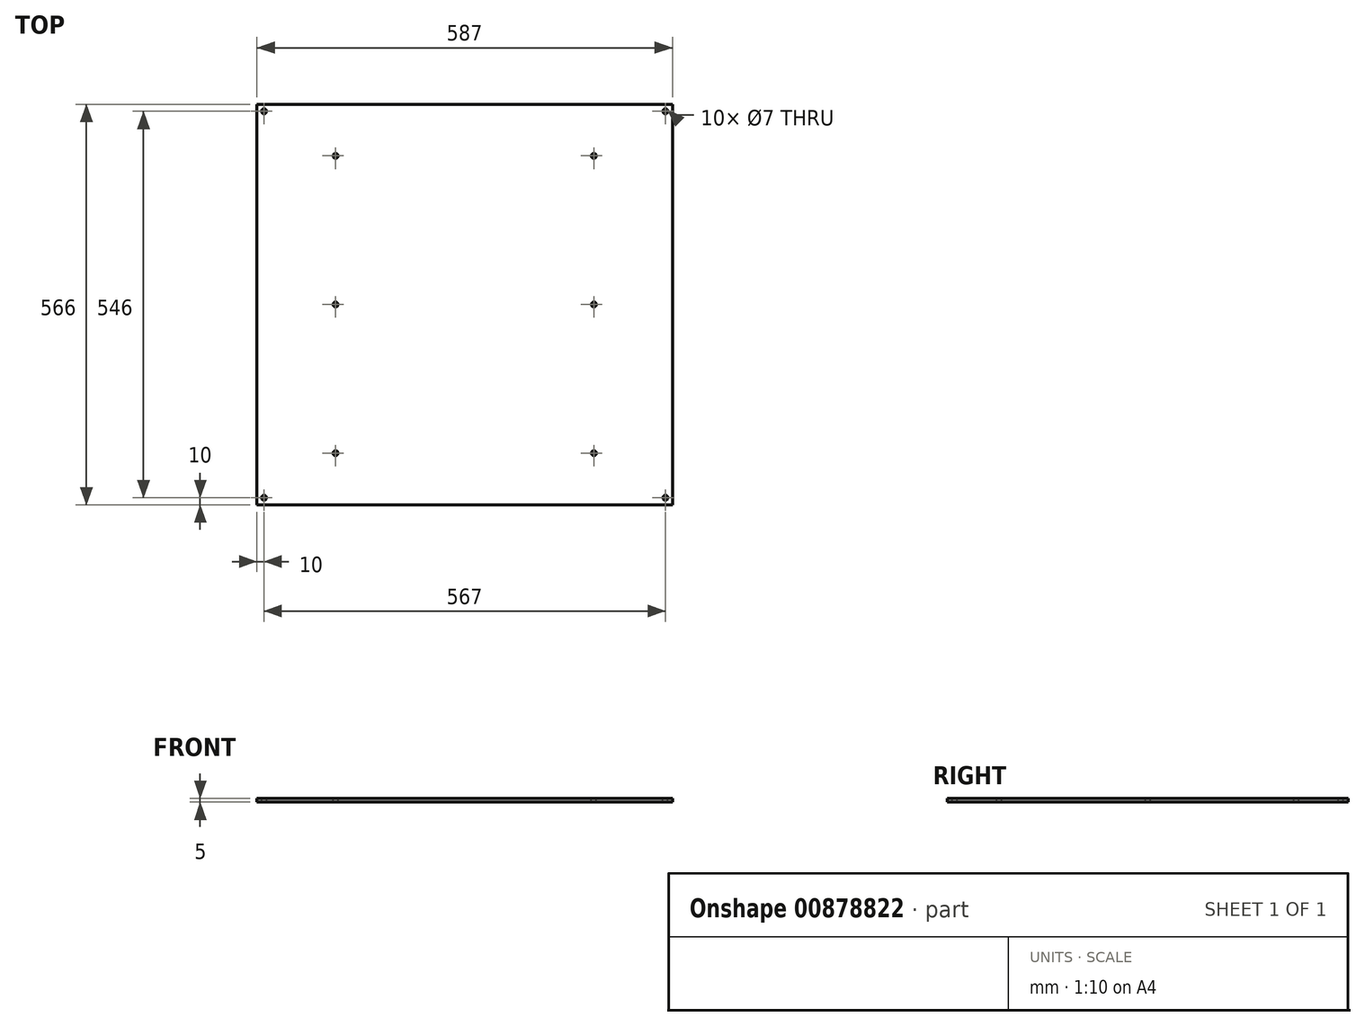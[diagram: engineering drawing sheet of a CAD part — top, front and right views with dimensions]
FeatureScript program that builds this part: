
annotation { "Feature Type Name" : "Feature", "Feature Type Description" : "" }
export const myFeature = defineFeature(function(context is Context, id is Id, definition is map)
    precondition{}
    {
        {
            var Q0;
            Q0=qCreatedBy(makeId("Top.planeOp"),FACE);
            var sketch = newSketch(context, id + "F0", { "sketchPlane" : qUnion([Q0])});
            skLineSegment(sketch, "E0.bottom", {"start": v(0, 0) * mm, "end": v(587, 0) * mm});
            skLineSegment(sketch, "E0.top", {"start": v(0, 566) * mm, "end": v(587, 566) * mm});
            skLineSegment(sketch, "E0.left", {"start": v(0, 0) * mm, "end": v(0, 566) * mm});
            skLineSegment(sketch, "E0.right", {"start": v(587, 0) * mm, "end": v(587, 566) * mm});
            skSolve(sketch);
        }
        {
            var Q0;
            Q0=makeQuery(id+"F0.imprint","IMPRINT",FACE,{"disambiguationData":[TD([[makeQuery(id+"F0.imprint","IMPRINT",EDGE,{"derivedFrom":sQuery(id+"F0.wireOp",EDGE,"E0.bottom")}),1.0]])]});
            extrude(context, id + "F1", {"entities" : qUnion([Q0]), "depth" : 5 * mm, "offsetDistance" : 25 * mm});
        }
        {
            var Q0;
            Q0=makeQuery(id+"F1.opExtrude","CAP_FACE",FACE,{"disambiguationData":[OSD([sQuery(id+"F0.wireOp",EDGE,"E0.bottom"),sQuery(id+"F0.wireOp",EDGE,"E0.top"),sQuery(id+"F0.wireOp",EDGE,"E0.left"),sQuery(id+"F0.wireOp",EDGE,"E0.right")])],"isStart":false});
            var sketch = newSketch(context, id + "F2", { "sketchPlane" : qUnion([Q0])});
            skCircle(sketch, "E1", {"center": v(10, 10) * mm, "radius": 3.5 * mm});
            skCircle(sketch, "E2", {"center": v(577, 10) * mm, "radius": 3.5 * mm});
            skCircle(sketch, "E3", {"center": v(10, 556) * mm, "radius": 3.5 * mm});
            skCircle(sketch, "E4", {"center": v(577, 556) * mm, "radius": 3.5 * mm});
            skSolve(sketch);
        }
        {
            var Q0;
            Q0=sQuery(id+"F2.wireOp",VERTEX,"E3.center");
            var Q1;
            Q1=sQuery(id+"F2.wireOp",VERTEX,"E4.center");
            var Q2;
            Q2=sQuery(id+"F2.wireOp",VERTEX,"E2.center");
            var Q3;
            Q3=sQuery(id+"F2.wireOp",VERTEX,"E1.center");
            var Q4;
            Q4=makeQuery(id+"F1.opExtrude","SWEPT_BODY",BODY,{"disambiguationData":[OSD([sQuery(id+"F0.wireOp",EDGE,"E0.bottom"),sQuery(id+"F0.wireOp",EDGE,"E0.top"),sQuery(id+"F0.wireOp",EDGE,"E0.left"),sQuery(id+"F0.wireOp",EDGE,"E0.right")])]});
            hole(context, id + "F3", {"style" : HoleStyle.SIMPLE, "endStyle" : HoleEndStyle.THROUGH, "holeDiameter" : 7 * mm, "majorDiameter" : 5 * mm, "isTappedThrough" : true, "tappedDepth" : 12 * mm, "tapClearance" : 3, "locations" : qUnion([Q0, Q1, Q2, Q3]), "scope" : qUnion([Q4])});
        }
        {
            var Q0;
            Q0=makeQuery(id+"F1.opExtrude","CAP_FACE",FACE,{"disambiguationData":[OSD([sQuery(id+"F0.wireOp",EDGE,"E0.bottom"),sQuery(id+"F0.wireOp",EDGE,"E0.top"),sQuery(id+"F0.wireOp",EDGE,"E0.left"),sQuery(id+"F0.wireOp",EDGE,"E0.right")])],"isStart":false});
            var sketch = newSketch(context, id + "F4", { "sketchPlane" : qUnion([Q0])});
            skLineSegment(sketch, "E5", {"start": v(293.5, 566) * mm, "end": v(293.5, 0) * mm, "construction": true});
            skLineSegment(sketch, "E6", {"start": v(0, 283) * mm, "end": v(587, 283) * mm, "construction": true});
            skLineSegment(sketch, "E7", {"start": v(111, 566) * mm, "end": v(111, 0) * mm, "construction": true});
            skLineSegment(sketch, "E8.MirrorCS", {"start": v(476, 566) * mm, "end": v(476, 0) * mm, "construction": true});
            skLineSegment(sketch, "E9", {"start": v(0, 493) * mm, "end": v(587, 493) * mm, "construction": true});
            skLineSegment(sketch, "E10.MirrorCS", {"start": v(0, 73) * mm, "end": v(587, 73) * mm, "construction": true});
            skCircle(sketch, "E11", {"center": v(111, 493) * mm, "radius": 3.5 * mm});
            skCircle(sketch, "E12", {"center": v(476, 493) * mm, "radius": 3.5 * mm});
            skCircle(sketch, "E13", {"center": v(111, 73) * mm, "radius": 3.5 * mm});
            skCircle(sketch, "E14.MirrorC", {"center": v(476, 73) * mm, "radius": 3.5 * mm});
            skCircle(sketch, "E15", {"center": v(111, 283) * mm, "radius": 3.5 * mm});
            skCircle(sketch, "E16.MirrorC", {"center": v(476, 283) * mm, "radius": 3.5 * mm});
            skSolve(sketch);
        }
        {
            var Q0;
            Q0=sQuery(id+"F4.wireOp",VERTEX,"E11.center");
            var Q1;
            Q1=sQuery(id+"F4.wireOp",VERTEX,"E12.center");
            var Q2;
            Q2=sQuery(id+"F4.wireOp",VERTEX,"E15.center");
            var Q3;
            Q3=sQuery(id+"F4.wireOp",VERTEX,"E16.MirrorC.center");
            var Q4;
            Q4=sQuery(id+"F4.wireOp",VERTEX,"E13.center");
            var Q5;
            Q5=sQuery(id+"F4.wireOp",VERTEX,"E14.MirrorC.center");
            var Q6;
            Q6=makeQuery(id+"F1.opExtrude","SWEPT_BODY",BODY,{"disambiguationData":[OSD([sQuery(id+"F0.wireOp",EDGE,"E0.bottom"),sQuery(id+"F0.wireOp",EDGE,"E0.top"),sQuery(id+"F0.wireOp",EDGE,"E0.left"),sQuery(id+"F0.wireOp",EDGE,"E0.right")])]});
            hole(context, id + "F5", {"style" : HoleStyle.SIMPLE, "endStyle" : HoleEndStyle.THROUGH, "holeDiameter" : 7 * mm, "majorDiameter" : 5 * mm, "isTappedThrough" : true, "tappedDepth" : 12 * mm, "tapClearance" : 3, "locations" : qUnion([Q0, Q1, Q2, Q3, Q4, Q5]), "scope" : qUnion([Q6])});
        }
    });
